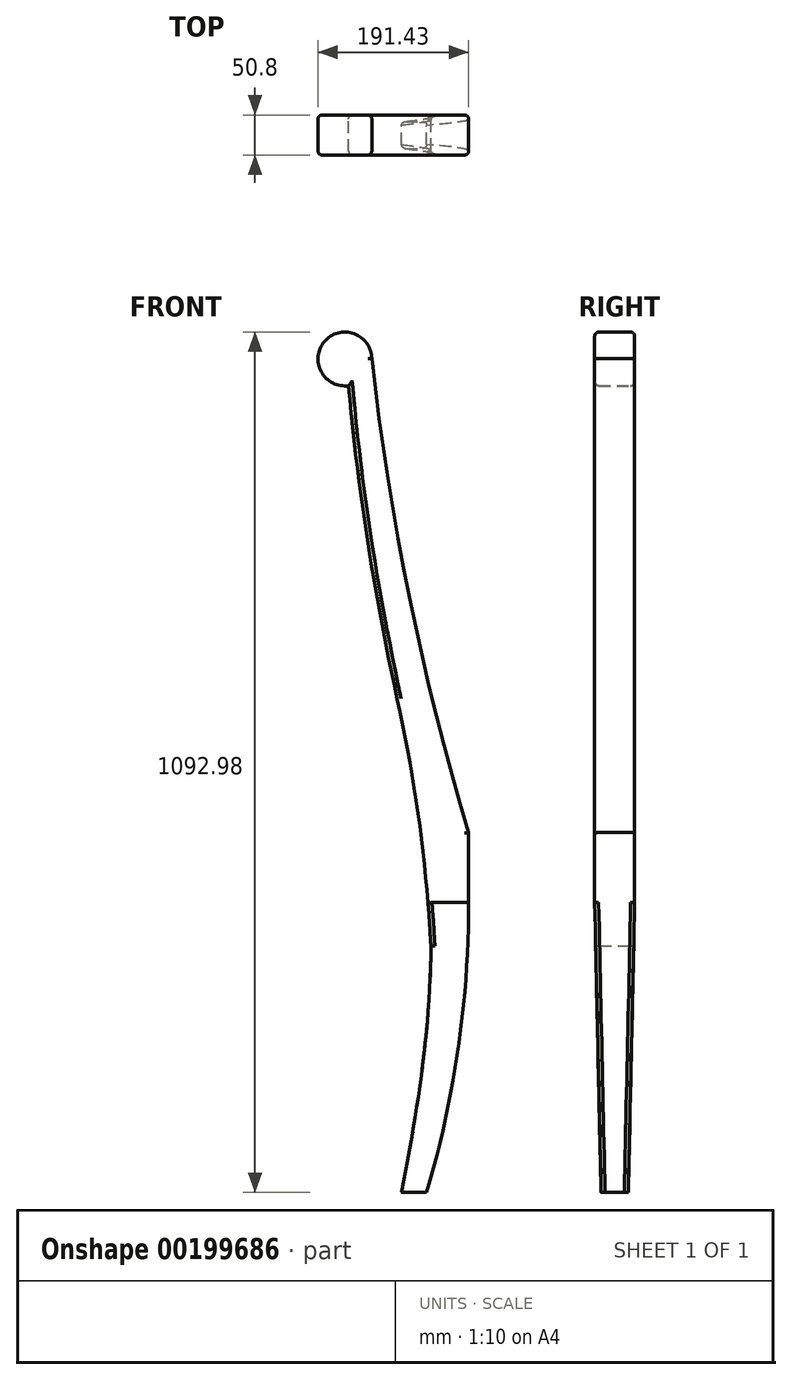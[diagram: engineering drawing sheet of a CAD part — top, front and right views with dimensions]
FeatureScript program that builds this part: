
annotation { "Feature Type Name" : "Feature", "Feature Type Description" : "" }
export const myFeature = defineFeature(function(context is Context, id is Id, definition is map)
    precondition{}
    {
        {
            var Q0;
            Q0=qCreatedBy(makeId("Front.planeOp"),FACE);
            var sketch = newSketch(context, id + "F0", { "sketchPlane" : qUnion([Q0])});
            skLineSegment(sketch, "E0", {"start": v(0, 0) * mm, "end": v(0, 1066.8) * mm, "construction": true});
            skArc(sketch, "E1", {"start": v(60.06, 1059.4) * mm, "mid": v(-0.08, 1081.04) * mm, "end": v(30.53, 1024.93) * mm});
            skArc(sketch, "E2", {"start": v(60.06, 1059.4) * mm, "mid": v(107.99, 755.52) * mm, "end": v(183.13, 457.2) * mm});
            skLineSegment(sketch, "E3", {"start": v(183.13, 457.2) * mm, "end": v(183.13, 368.3) * mm});
            skArc(sketch, "E4", {"start": v(129.64, 0) * mm, "mid": v(169.69, 182.22) * mm, "end": v(183.13, 368.3) * mm});
            skLineSegment(sketch, "E5", {"start": v(129.64, 0) * mm, "end": v(97.89, 0) * mm});
            skFitSpline(sketch, "E6", {"points": [v(30.53, 1024.93) * mm, v(132.33, 457.2) * mm], "startDerivative": vector(54.14, -601.72) * mm, "endDerivative": vector(146.8, -580.35) * mm});
            skFitSpline(sketch, "E7", {"points": [v(97.89, 0) * mm, v(132.33, 368.3) * mm], "startDerivative": vector(66.75, 338.99) * mm, "endDerivative": vector(-32.18, 318.78) * mm});
            skArc(sketch, "E8", {"start": v(135.04, 313.25) * mm, "mid": v(120.28, 470.88) * mm, "end": v(92.29, 626.7) * mm});
            skSolve(sketch);
        }
        {
            var Q0;
            Q0=makeQuery(id+"F0.imprint","IMPRINT",FACE,{"disambiguationData":[TD([[makeQuery(id+"F0.imprint","IMPRINT",EDGE,{"derivedFrom":sQuery(id+"F0.wireOp",EDGE,"E1")}),1.0]])]});
            extrude(context, id + "F1", {"entities" : qUnion([Q0]), "depth" : 50.8 * mm});
        }
        {
            var Q0;
            Q0=makeQuery(id+"F1.opExtrude","SWEPT_FACE",FACE,{"disambiguationData":[OSD([sQuery(id+"F0.wireOp",EDGE,"E3")])]});
            var sketch = newSketch(context, id + "F2", { "sketchPlane" : qUnion([Q0])});
            skLineSegment(sketch, "E9", {"start": v(-50.8, 368.3) * mm, "end": v(-42.67, 0) * mm});
            skLineSegment(sketch, "E10", {"start": v(-42.67, 0) * mm, "end": v(-50.8, -0.18) * mm});
            skLineSegment(sketch, "E11", {"start": v(-50.8, -0.18) * mm, "end": v(-50.8, 368.3) * mm});
            skLineSegment(sketch, "E12", {"start": v(0, 368.3) * mm, "end": v(-8.13, 0) * mm});
            skLineSegment(sketch, "E13", {"start": v(-8.13, 0) * mm, "end": v(0, 0) * mm});
            skLineSegment(sketch, "E14", {"start": v(0, 0) * mm, "end": v(0, 368.3) * mm});
            skSolve(sketch);
        }
        {
            var Q0;
            Q0=makeQuery(id+"F2.imprint","IMPRINT",FACE,{"disambiguationData":[TD([[makeQuery(id+"F2.imprint","IMPRINT",EDGE,{"derivedFrom":sQuery(id+"F2.wireOp",EDGE,"E9")}),-1.0]])]});
            var Q1;
            Q1=makeQuery(id+"F2.imprint","IMPRINT",FACE,{"disambiguationData":[TD([[makeQuery(id+"F2.imprint","IMPRINT",EDGE,{"derivedFrom":sQuery(id+"F2.wireOp",EDGE,"E12")}),1.0]])]});
            extrude(context, id + "F3", {"entities" : qUnion([Q0, Q1]), "operationType" : NewBodyOperationType.REMOVE, "endBound" : BoundingType.THROUGH_ALL, "oppositeDirection" : true, "depth" : 25.4 * mm});
        }
        {
            var Q0;
            Q0=makeQuery(id+"F1.opExtrude","CAP_EDGE",EDGE,{"disambiguationData":[OSD([sQuery(id+"F0.wireOp",EDGE,"E8")])],"isStart":true});
            var Q1;
            Q1=makeQuery(id+"F1.opExtrude","CAP_EDGE",EDGE,{"disambiguationData":[OSD([sQuery(id+"F0.wireOp",EDGE,"E6")])],"isStart":true});
            var Q2;
            Q2=makeQuery(id+"F1.opExtrude","CAP_EDGE",EDGE,{"disambiguationData":[OSD([sQuery(id+"F0.wireOp",EDGE,"E8")])],"isStart":false});
            var Q3;
            Q3=makeQuery(id+"F1.opExtrude","CAP_EDGE",EDGE,{"disambiguationData":[OSD([sQuery(id+"F0.wireOp",EDGE,"E6")])],"isStart":false});
            var Q4;
            Q4=makeQuery(id+"F1.opExtrude","CAP_EDGE",EDGE,{"disambiguationData":[OSD([sQuery(id+"F0.wireOp",EDGE,"E2")])],"isStart":false});
            var Q5;
            Q5=makeQuery(id+"F1.opExtrude","CAP_EDGE",EDGE,{"disambiguationData":[OSD([sQuery(id+"F0.wireOp",EDGE,"E2")])],"isStart":true});
            var Q6;
            Q6=makeQuery(id+"F1.opExtrude","CAP_EDGE",EDGE,{"disambiguationData":[OSD([sQuery(id+"F0.wireOp",EDGE,"E3")])],"isStart":false});
            var Q7;
            Q7=makeQuery(id+"F3.boolean.opBoolean","INTERSECT",EDGE,{"derivedFrom":[makeQuery(id+"F1.opExtrude","SWEPT_FACE",FACE,{"disambiguationData":[OSD([sQuery(id+"F0.wireOp",EDGE,"E4")])]}),makeQuery(id+"F3.opExtrude","SWEPT_FACE",FACE,{"disambiguationData":[OSD([sQuery(id+"F2.wireOp",EDGE,"E9")])]})]});
            var Q8;
            Q8=makeQuery(id+"F1.opExtrude","CAP_EDGE",EDGE,{"disambiguationData":[OSD([sQuery(id+"F0.wireOp",EDGE,"E3")])],"isStart":true});
            var Q9;
            Q9=makeQuery(id+"F3.boolean.opBoolean","INTERSECT",EDGE,{"derivedFrom":[makeQuery(id+"F1.opExtrude","SWEPT_FACE",FACE,{"disambiguationData":[OSD([sQuery(id+"F0.wireOp",EDGE,"E4")])]}),makeQuery(id+"F3.opExtrude","SWEPT_FACE",FACE,{"disambiguationData":[OSD([sQuery(id+"F2.wireOp",EDGE,"E12")])]})]});
            var Q10;
            Q10=makeQuery(id+"F1.opExtrude","CAP_EDGE",EDGE,{"disambiguationData":[OSD([sQuery(id+"F0.wireOp",EDGE,"E1")])],"isStart":true});
            var Q11;
            Q11=makeQuery(id+"F1.opExtrude","CAP_EDGE",EDGE,{"disambiguationData":[OSD([sQuery(id+"F0.wireOp",EDGE,"E1")])],"isStart":false});
            fillet(context, id + "F4", {"entities" : qUnion([Q0, Q1, Q2, Q3, Q4, Q5, Q6, Q7, Q8, Q9, Q10, Q11]), "radius" : 5.08 * mm, "tangentPropagation" : true, "allowEdgeOverflow" : false});
        }
    });
